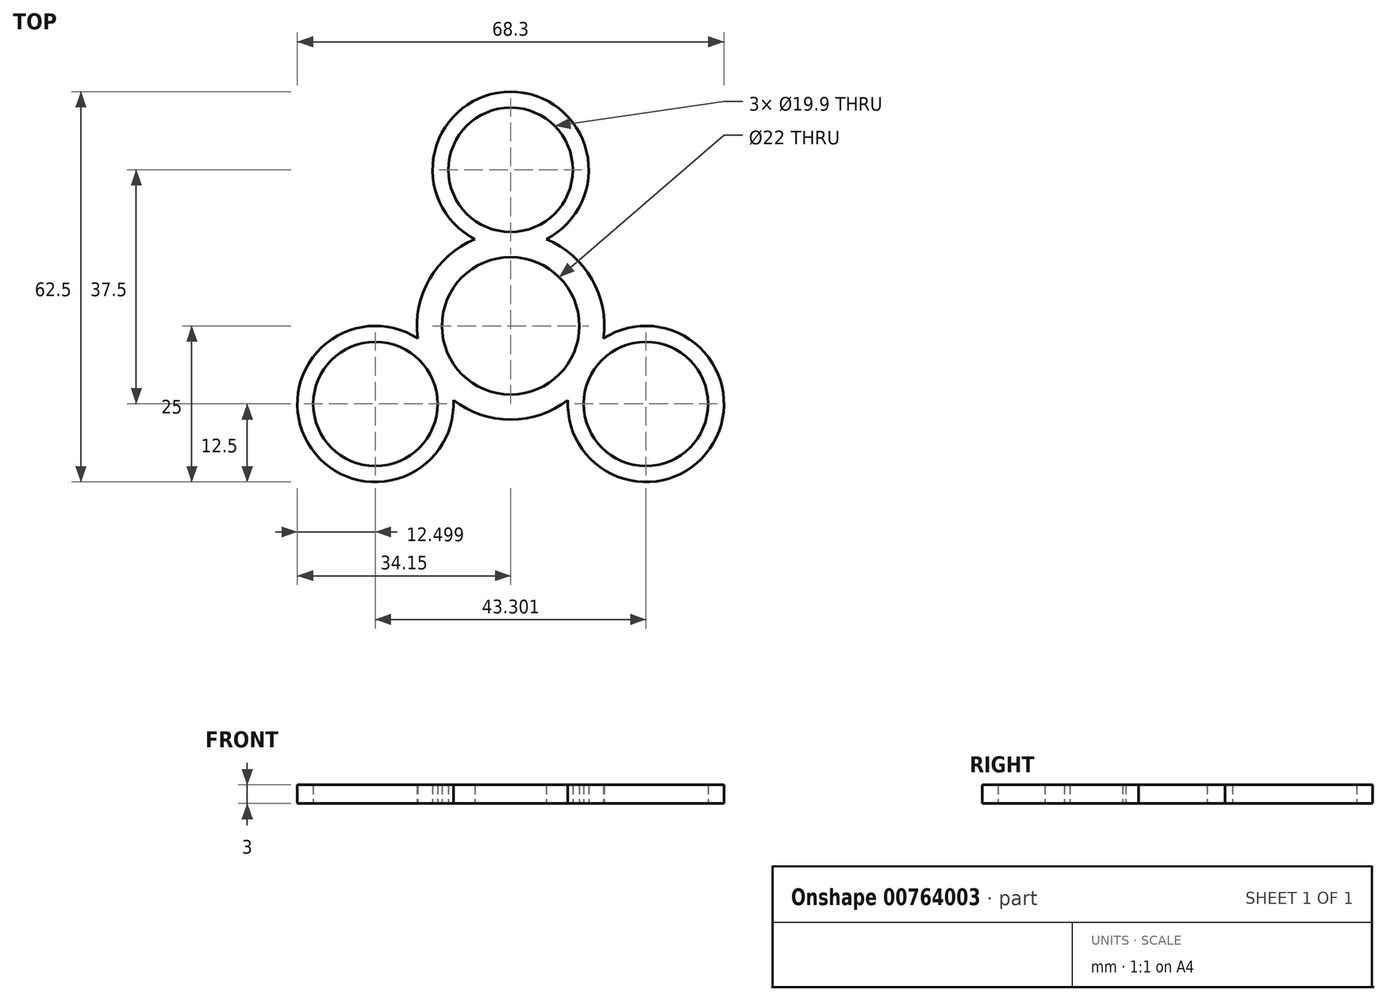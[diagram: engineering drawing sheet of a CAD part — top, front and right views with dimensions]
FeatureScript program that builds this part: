
annotation { "Feature Type Name" : "Feature", "Feature Type Description" : "" }
export const myFeature = defineFeature(function(context is Context, id is Id, definition is map)
    precondition{}
    {
        {
            var Q0;
            Q0=qCreatedBy(makeId("Top.planeOp"),FACE);
            var sketch = newSketch(context, id + "F0", { "sketchPlane" : qUnion([Q0])});
            skArc(sketch, "E0", {"start": v(9.53, 5.5) * mm, "mid": v(0, 11) * mm, "end": v(-9.53, 5.5) * mm});
            skCircle(sketch, "E1", {"center": v(0, 25) * mm, "radius": 9.95 * mm});
            skArc(sketch, "E2", {"start": v(-5.7, 13.87) * mm, "mid": v(-9.87, 11.3) * mm, "end": v(-13, 7.5) * mm});
            skArc(sketch, "E3", {"start": v(5.7, 13.88) * mm, "mid": v(0, 37.5) * mm, "end": v(-5.7, 13.88) * mm});
            skArc(sketch, "E4.trimOffspring", {"start": v(13, 7.5) * mm, "mid": v(9.87, 11.3) * mm, "end": v(5.7, 13.87) * mm});
            skCircle(sketch, "E5.1.0", {"center": v(-21.65, -12.5) * mm, "radius": 9.95 * mm});
            skArc(sketch, "E5.1.1", {"start": v(-14.87, -2) * mm, "mid": v(-32.48, -18.75) * mm, "end": v(-9.17, -11.87) * mm});
            skArc(sketch, "E5.1.2", {"start": v(-13, 7.5) * mm, "mid": v(-14.72, 2.9) * mm, "end": v(-14.87, -2) * mm});
            skArc(sketch, "E5.1.3", {"start": v(-9.53, 5.5) * mm, "mid": v(-9.53, -5.5) * mm, "end": v(0, -11) * mm});
            skArc(sketch, "E5.1.4", {"start": v(-9.17, -11.87) * mm, "mid": v(-4.84, -14.2) * mm, "end": v(0, -15) * mm});
            skCircle(sketch, "E5.2.0", {"center": v(21.65, -12.5) * mm, "radius": 9.95 * mm});
            skArc(sketch, "E5.2.1", {"start": v(9.17, -11.87) * mm, "mid": v(32.48, -18.75) * mm, "end": v(14.87, -2) * mm});
            skArc(sketch, "E5.2.2", {"start": v(0, -15) * mm, "mid": v(4.84, -14.2) * mm, "end": v(9.17, -11.87) * mm});
            skArc(sketch, "E5.2.3", {"start": v(0, -11) * mm, "mid": v(9.53, -5.5) * mm, "end": v(9.53, 5.5) * mm});
            skArc(sketch, "E5.2.4", {"start": v(14.87, -2) * mm, "mid": v(14.72, 2.9) * mm, "end": v(13, 7.5) * mm});
            skSolve(sketch);
        }
        {
            var Q0;
            Q0 = qSketchRegion(id + "F0", true);
            extrude(context, id + "F1", {"entities" : qUnion([Q0]), "depth" : 3 * mm, "offsetDistance" : 25 * mm});
        }
    });
